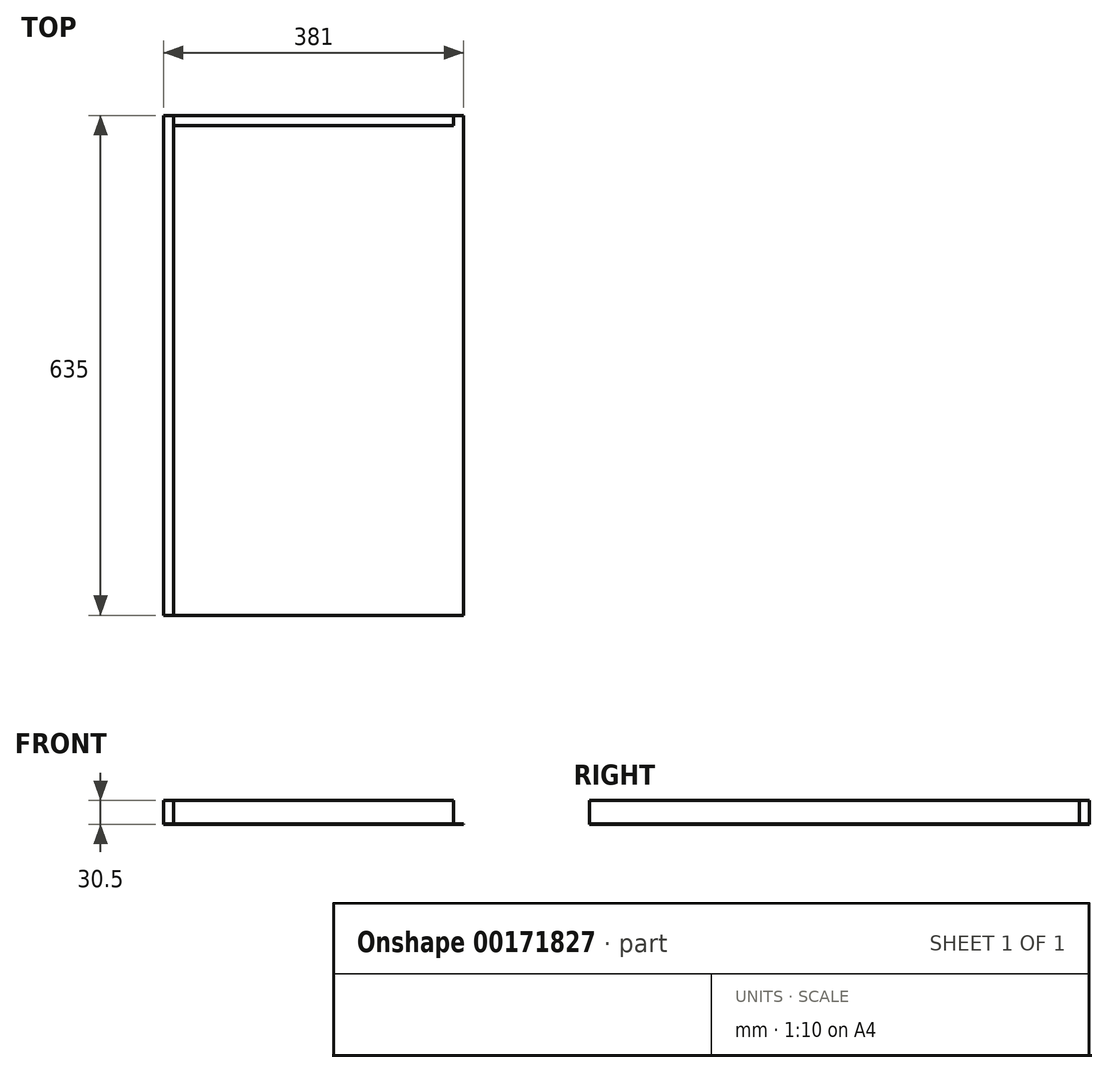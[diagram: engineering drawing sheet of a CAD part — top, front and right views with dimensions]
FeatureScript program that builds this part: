
annotation { "Feature Type Name" : "Feature", "Feature Type Description" : "" }
export const myFeature = defineFeature(function(context is Context, id is Id, definition is map)
    precondition{}
    {
        {
            var Q0;
            Q0=qCreatedBy(makeId("Top.planeOp"),FACE);
            var sketch = newSketch(context, id + "F0", { "sketchPlane" : qUnion([Q0])});
            skLineSegment(sketch, "E0.bottom", {"start": v(190.5, 317.5) * mm, "end": v(-190.5, 317.5) * mm});
            skLineSegment(sketch, "E0.top", {"start": v(190.5, -317.5) * mm, "end": v(-190.5, -317.5) * mm});
            skLineSegment(sketch, "E0.left", {"start": v(190.5, 317.5) * mm, "end": v(190.5, -317.5) * mm});
            skLineSegment(sketch, "E0.right", {"start": v(-190.5, 317.5) * mm, "end": v(-190.5, -317.5) * mm});
            skPoint(sketch, "E0.middle", {"position": v(0, 0) * mm});
            skSolve(sketch);
        }
        {
            assignVariable(context, id + "F1", {"name" : "board_thickness", "anyValue" : .5});
        }
        {
            assignVariable(context, id + "F2", {"name" : "drawers_height", "anyValue" : 30});
        }
        {
            var Q0;
            Q0 = qSketchRegion(id + "F0", true);
            extrude(context, id + "F3", {"entities" : qUnion([Q0]), "depth" : (getVariable(context, 'board_thickness')) * mm});
        }
        {
            var Q0;
            Q0=makeQuery(id+"F3.opExtrude","CAP_FACE",FACE,{"disambiguationData":[OSD([sQuery(id+"F0.wireOp",EDGE,"E0.bottom"),sQuery(id+"F0.wireOp",EDGE,"E0.top"),sQuery(id+"F0.wireOp",EDGE,"E0.left"),sQuery(id+"F0.wireOp",EDGE,"E0.right")])],"isStart":false});
            var sketch = newSketch(context, id + "F4", { "sketchPlane" : qUnion([Q0])});
            skLineSegment(sketch, "E1.bottom", {"start": v(-190.5, -317.5) * mm, "end": v(-177.8, -317.5) * mm});
            skLineSegment(sketch, "E1.top", {"start": v(-190.5, 317.5) * mm, "end": v(-177.8, 317.5) * mm});
            skLineSegment(sketch, "E1.left", {"start": v(-190.5, -317.5) * mm, "end": v(-190.5, 317.5) * mm});
            skLineSegment(sketch, "E1.right", {"start": v(-177.8, -317.5) * mm, "end": v(-177.8, 317.5) * mm});
            skLineSegment(sketch, "E2.bottom", {"start": v(-177.8, 317.5) * mm, "end": v(177.8, 317.5) * mm});
            skLineSegment(sketch, "E2.top", {"start": v(-177.8, 304.8) * mm, "end": v(177.8, 304.8) * mm});
            skLineSegment(sketch, "E2.left", {"start": v(-177.8, 317.5) * mm, "end": v(-177.8, 304.8) * mm});
            skLineSegment(sketch, "E2.right", {"start": v(177.8, 317.5) * mm, "end": v(177.8, 304.8) * mm});
            skSolve(sketch);
        }
        {
            var Q0;
            Q0=makeQuery(id+"F4.imprint","IMPRINT",FACE,{"disambiguationData":[TD([[makeQuery(id+"F4.imprint","IMPRINT",EDGE,{"derivedFrom":sQuery(id+"F4.wireOp",EDGE,"E1.bottom")}),-1.0]])]});
            extrude(context, id + "F5", {"entities" : qUnion([Q0]), "depth" : (getVariable(context, 'drawers_height')) * mm});
        }
        {
            var Q0;
            Q0=makeQuery(id+"F4.imprint","IMPRINT",FACE,{"disambiguationData":[TD([[makeQuery(id+"F4.imprint","IMPRINT",EDGE,{"derivedFrom":sQuery(id+"F4.wireOp",EDGE,"E2.bottom")}),1.0]])]});
            extrude(context, id + "F6", {"entities" : qUnion([Q0]), "depth" : (getVariable(context, 'drawers_height')) * mm});
        }
    });
